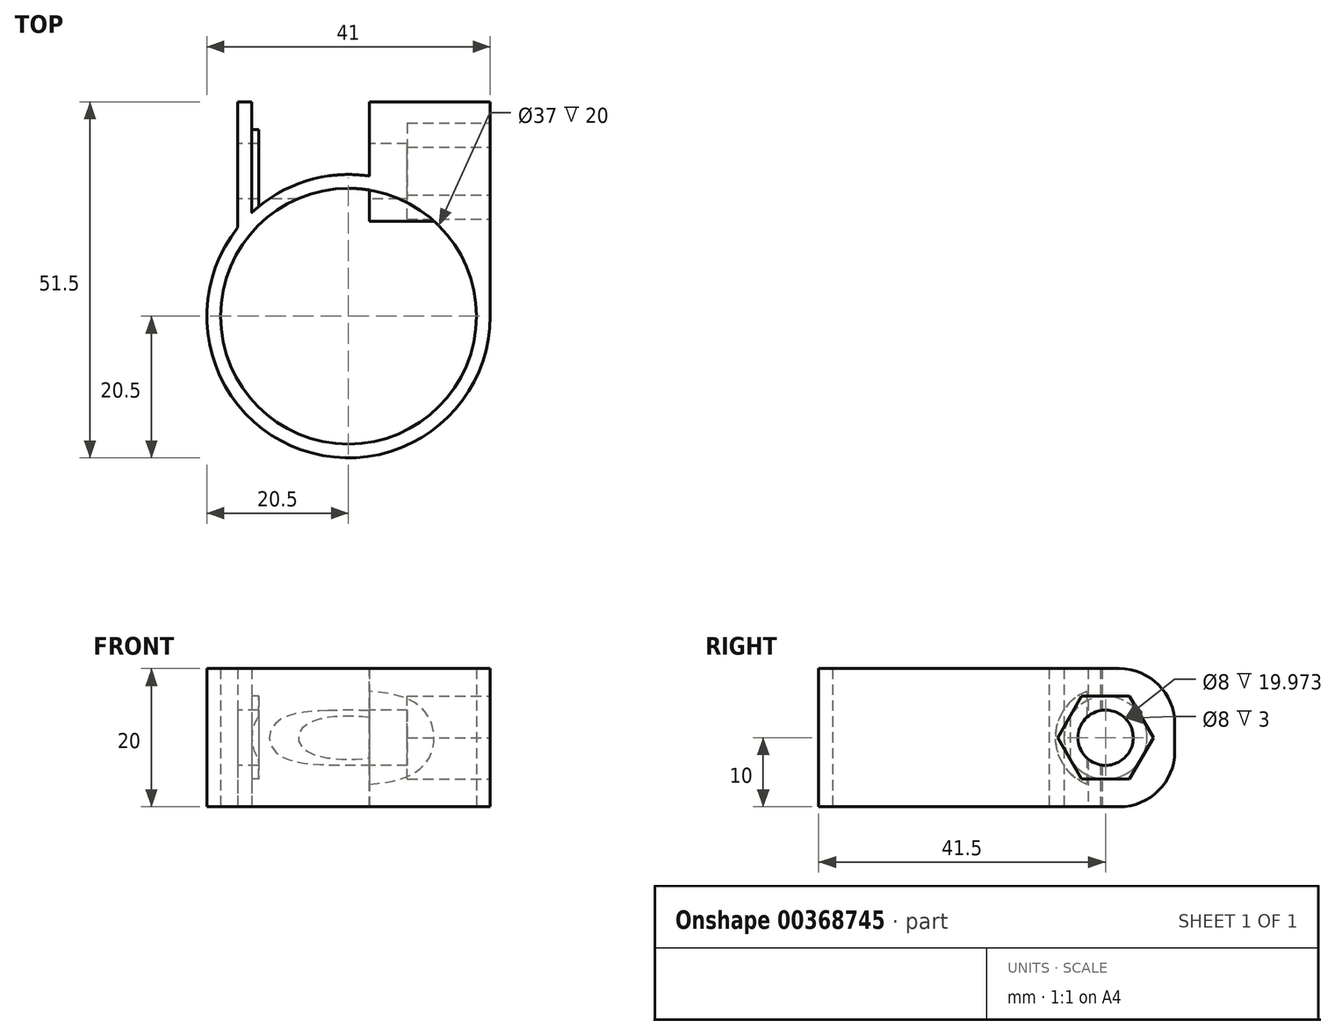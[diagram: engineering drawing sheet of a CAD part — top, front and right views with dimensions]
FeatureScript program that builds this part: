
annotation { "Feature Type Name" : "Feature", "Feature Type Description" : "" }
export const myFeature = defineFeature(function(context is Context, id is Id, definition is map)
    precondition{}
    {
        {
            var Q0;
            Q0=qCreatedBy(makeId("Top.planeOp"),FACE);
            var sketch = newSketch(context, id + "F0", { "sketchPlane" : qUnion([Q0])});
            skCircle(sketch, "E0", {"center": v(0, 0) * mm, "radius": 18.5 * mm});
            skLineSegment(sketch, "E1", {"start": v(-14, 12.1) * mm, "end": v(14, 12.1) * mm, "construction": true});
            skLineSegment(sketch, "E2.bottom", {"start": v(-14, 9.29) * mm, "end": v(-16, 9.29) * mm});
            skLineSegment(sketch, "E2.top", {"start": v(-14, 31) * mm, "end": v(-16, 31) * mm});
            skLineSegment(sketch, "E2.left", {"start": v(-14, 9.29) * mm, "end": v(-14, 31) * mm});
            skLineSegment(sketch, "E2.right", {"start": v(-16, 9.29) * mm, "end": v(-16, 31) * mm});
            skCircle(sketch, "E3", {"center": v(0, 0) * mm, "radius": 20.5 * mm});
            skLineSegment(sketch, "E4.MirrorCS", {"start": v(16, 9.29) * mm, "end": v(16, 31) * mm});
            skLineSegment(sketch, "E5.bottom", {"start": v(16, 31) * mm, "end": v(20.5, 31) * mm});
            skLineSegment(sketch, "E5.top", {"start": v(16, 0) * mm, "end": v(20.5, 0) * mm});
            skLineSegment(sketch, "E5.left", {"start": v(16, 31) * mm, "end": v(16, 0) * mm});
            skLineSegment(sketch, "E5.right", {"start": v(20.5, 31) * mm, "end": v(20.5, 0) * mm});
            skLineSegment(sketch, "E6.bottom", {"start": v(16, 31) * mm, "end": v(3, 31) * mm});
            skLineSegment(sketch, "E6.top", {"start": v(16, 9.29) * mm, "end": v(3, 9.29) * mm});
            skLineSegment(sketch, "E6.left", {"start": v(16, 31) * mm, "end": v(16, 9.29) * mm});
            skLineSegment(sketch, "E6.right", {"start": v(3, 31) * mm, "end": v(3, 9.29) * mm});
            skSolve(sketch);
        }
        {
            var Q0;
            {var subQ0=sQuery(id+"F0.wireOp",EDGE,"E2.right");var subQ5=sQuery(id+"F0.wireOp",EDGE,"E3");var subQ7=makeQuery(id+"F0.imprint","INTERSECT",VERTEX,{"derivedFrom":[subQ0,subQ5]});Q0=makeQuery(id+"F0.imprint","IMPRINT",FACE,{"disambiguationData":[TD([[makeQuery(id+"F0.imprint","IMPRINT",EDGE,{"disambiguationData":[TD([[subQ7,-1.0]])],"derivedFrom":subQ5}),1.0]])]});}
            var Q1;
            {var subQ0=sQuery(id+"F0.wireOp",EDGE,"E2.top");Q1=makeQuery(id+"F0.imprint","IMPRINT",FACE,{"disambiguationData":[TD([[makeQuery(id+"F0.imprint","IMPRINT",EDGE,{"derivedFrom":subQ0}),1.0]])]});}
            var Q2;
            {var subQ3=sQuery(id+"F0.wireOp",EDGE,"E2.left");var subQ5=sQuery(id+"F0.wireOp",EDGE,"E3");var subQ6=makeQuery(id+"F0.imprint","INTERSECT",VERTEX,{"derivedFrom":[subQ3,subQ5]});Q2=makeQuery(id+"F0.imprint","IMPRINT",FACE,{"disambiguationData":[TD([[makeQuery(id+"F0.imprint","IMPRINT",EDGE,{"disambiguationData":[TD([[subQ6,1.0]])],"derivedFrom":subQ3}),1.0]])]});}
            var Q3;
            {var subQ5=sQuery(id+"F0.wireOp",EDGE,"bf74c628-281e-4c9b-bb8e-f0f7317052d90.MirrorCS");Q3=makeQuery(id+"F0.imprint","IMPRINT",FACE,{"disambiguationData":[TD([[makeQuery(id+"F0.imprint","IMPRINT",EDGE,{"derivedFrom":subQ5}),-1.0]])]});}
            var Q4;
            {var subQ4=sQuery(id+"F0.wireOp",EDGE,"E5.bottom");Q4=makeQuery(id+"F0.imprint","IMPRINT",FACE,{"disambiguationData":[TD([[makeQuery(id+"F0.imprint","IMPRINT",EDGE,{"derivedFrom":subQ4}),-1.0]])]});}
            var Q5;
            {var subQ1=sQuery(id+"F0.wireOp",EDGE,"E0");var subQ3=sQuery(id+"F0.wireOp",EDGE,"E5.top");var subQ4=makeQuery(id+"F0.imprint","INTERSECT",VERTEX,{"derivedFrom":[subQ1,subQ3]});Q5=makeQuery(id+"F0.imprint","IMPRINT",FACE,{"disambiguationData":[TD([[makeQuery(id+"F0.imprint","IMPRINT",EDGE,{"disambiguationData":[TD([[subQ4,-1.0]])],"derivedFrom":subQ1}),-1.0]])]});}
            var Q6;
            {var subQ5=sQuery(id+"F0.wireOp",EDGE,"E6.bottom");Q6=makeQuery(id+"F0.imprint","IMPRINT",FACE,{"disambiguationData":[TD([[makeQuery(id+"F0.imprint","IMPRINT",EDGE,{"derivedFrom":subQ5}),1.0]])]});}
            var Q7;
            {var subQ0=sQuery(id+"F0.wireOp",EDGE,"E6.left");var subQ5=sQuery(id+"F0.wireOp",EDGE,"E3");var subQ6=makeQuery(id+"F0.imprint","INTERSECT",VERTEX,{"derivedFrom":[subQ5,subQ0]});Q7=makeQuery(id+"F0.imprint","IMPRINT",FACE,{"disambiguationData":[TD([[makeQuery(id+"F0.imprint","IMPRINT",EDGE,{"disambiguationData":[TD([[subQ6,1.0]])],"derivedFrom":subQ5}),1.0]])]});}
            var Q8;
            {var subQ3=sQuery(id+"F0.wireOp",EDGE,"E6.right");var subQ5=sQuery(id+"F0.wireOp",EDGE,"E3");var subQ6=makeQuery(id+"F0.imprint","INTERSECT",VERTEX,{"derivedFrom":[subQ5,subQ3]});Q8=makeQuery(id+"F0.imprint","IMPRINT",FACE,{"disambiguationData":[TD([[makeQuery(id+"F0.imprint","IMPRINT",EDGE,{"disambiguationData":[TD([[subQ6,1.0]])],"derivedFrom":subQ5}),1.0]])]});}
            var Q9;
            {var subQ3=sQuery(id+"F0.wireOp",EDGE,"E2.left");var subQ5=sQuery(id+"F0.wireOp",EDGE,"E3");var subQ6=makeQuery(id+"F0.imprint","INTERSECT",VERTEX,{"derivedFrom":[subQ3,subQ5]});Q9=makeQuery(id+"F0.imprint","IMPRINT",FACE,{"disambiguationData":[TD([[makeQuery(id+"F0.imprint","IMPRINT",EDGE,{"disambiguationData":[TD([[subQ6,1.0]])],"derivedFrom":subQ3}),1.0]])]});}
            extrude(context, id + "F1", {"entities" : qUnion([Q0, Q1, Q2, Q3, Q4, Q5, Q6, Q7, Q8, Q9]), "depth" : 20 * mm, "offsetDistance" : 25 * mm});
        }
        {
            var Q0;
            Q0=makeQuery(id+"F1.opExtrude","SWEPT_FACE",FACE,{"disambiguationData":[OSD([sQuery(id+"F0.wireOp",EDGE,"E2.right")])]});
            var sketch = newSketch(context, id + "F2", { "sketchPlane" : qUnion([Q0])});
            skLineSegment(sketch, "E7", {"start": v(-21, -7.76) * mm, "end": v(-21, 30.4) * mm, "construction": true});
            skLineSegment(sketch, "E8", {"start": v(-36.36, 10) * mm, "end": v(17.27, 10) * mm, "construction": true});
            skPoint(sketch, "E8.startSnap0", {"position": v(-31, 10) * mm});
            skCircle(sketch, "E9", {"center": v(-21, 10) * mm, "radius": 4 * mm});
            skCircle(sketch, "E10", {"center": v(-21, 10) * mm, "radius": 6 * mm});
            skSolve(sketch);
        }
        {
            var Q0;
            Q0=makeQuery(id+"F2.imprint","IMPRINT",FACE,{"disambiguationData":[TD([[makeQuery(id+"F2.imprint","IMPRINT",EDGE,{"derivedFrom":sQuery(id+"F2.wireOp",EDGE,"E9")}),1.0]])]});
            extrude(context, id + "F3", {"entities" : qUnion([Q0]), "operationType" : NewBodyOperationType.REMOVE, "oppositeDirection" : true, "depth" : 40 * mm, "offsetDistance" : 25 * mm});
        }
        {
            var Q0;
            Q0=makeQuery(id+"F2.imprint","IMPRINT",FACE,{"disambiguationData":[TD([[makeQuery(id+"F2.imprint","IMPRINT",EDGE,{"derivedFrom":sQuery(id+"F2.wireOp",EDGE,"E9")}),-1.0]])]});
            extrude(context, id + "F4", {"entities" : qUnion([Q0]), "operationType" : NewBodyOperationType.ADD, "oppositeDirection" : true, "depth" : 3 * mm, "offsetDistance" : 25 * mm});
        }
        {
            var Q0;
            Q0=makeQuery(id+"F1.opExtrude","SWEPT_FACE",FACE,{"disambiguationData":[OSD([sQuery(id+"F0.wireOp",EDGE,"E5.right")])]});
            var sketch = newSketch(context, id + "F5", { "sketchPlane" : qUnion([Q0])});
            skCircle(sketch, "E11.cCircle", {"center": v(21, 10) * mm, "radius": 6 * mm, "construction": true});
            skLineSegment(sketch, "E11.0", {"start": v(17.54, 16) * mm, "end": v(24.46, 16) * mm});
            skLineSegment(sketch, "E11.1", {"start": v(24.46, 16) * mm, "end": v(27.93, 10) * mm});
            skLineSegment(sketch, "E11.2", {"start": v(27.93, 10) * mm, "end": v(24.46, 4) * mm});
            skLineSegment(sketch, "E11.3", {"start": v(24.46, 4) * mm, "end": v(17.54, 4) * mm});
            skLineSegment(sketch, "E11.4", {"start": v(17.54, 4) * mm, "end": v(14.07, 10) * mm});
            skLineSegment(sketch, "E11.5", {"start": v(14.07, 10) * mm, "end": v(17.54, 16) * mm});
            skPoint(sketch, "E11.0.midPoint", {"position": v(21, 16) * mm});
            skCircle(sketch, "E12", {"center": v(21, 10) * mm, "radius": 7.25 * mm});
            skSolve(sketch);
        }
        {
            var Q0;
            Q0=makeQuery(id+"F5.imprint","IMPRINT",FACE,{"disambiguationData":[TD([[makeQuery(id+"F5.imprint","IMPRINT",EDGE,{"derivedFrom":sQuery(id+"F5.wireOp",EDGE,"E11.0")}),1.0]])]});
            var Q1;
            Q1=makeQuery(id+"F5.imprint","IMPRINT",FACE,{"disambiguationData":[TD([[makeQuery(id+"F5.imprint","IMPRINT",EDGE,{"derivedFrom":sQuery(id+"F5.wireOp",EDGE,"E11.0")}),-1.0]])]});
            extrude(context, id + "F6", {"entities" : qUnion([Q0, Q1]), "operationType" : NewBodyOperationType.ADD, "oppositeDirection" : true, "depth" : 17.5 * mm, "offsetDistance" : 25 * mm});
        }
        {
            var Q0;
            Q0=makeQuery(id+"F5.imprint","IMPRINT",FACE,{"disambiguationData":[TD([[makeQuery(id+"F5.imprint","IMPRINT",EDGE,{"derivedFrom":sQuery(id+"F5.wireOp",EDGE,"E11.0")}),-1.0]])]});
            extrude(context, id + "F7", {"entities" : qUnion([Q0]), "operationType" : NewBodyOperationType.REMOVE, "oppositeDirection" : true, "depth" : 12 * mm, "offsetDistance" : 25 * mm});
        }
        {
            var Q0;
            Q0=makeQuery(id+"F1.opExtrude","CAP_EDGE",EDGE,{"disambiguationData":[OSD([sQuery(id+"F0.wireOp",EDGE,"E5.bottom"),sQuery(id+"F0.wireOp",EDGE,"E6.bottom")])],"isStart":false});
            var Q1;
            Q1=makeQuery(id+"F1.opExtrude","CAP_EDGE",EDGE,{"disambiguationData":[OSD([sQuery(id+"F0.wireOp",EDGE,"E2.top")])],"isStart":false});
            var Q2;
            Q2=makeQuery(id+"F1.opExtrude","CAP_EDGE",EDGE,{"disambiguationData":[OSD([sQuery(id+"F0.wireOp",EDGE,"E5.bottom"),sQuery(id+"F0.wireOp",EDGE,"E6.bottom")])],"isStart":true});
            var Q3;
            Q3=makeQuery(id+"F1.opExtrude","CAP_EDGE",EDGE,{"disambiguationData":[OSD([sQuery(id+"F0.wireOp",EDGE,"E2.top")])],"isStart":true});
            fillet(context, id + "F8", {"entities" : qUnion([Q0, Q1, Q2, Q3]), "radius" : 8 * mm, "tangentPropagation" : true, "allowEdgeOverflow" : false});
        }
    });
